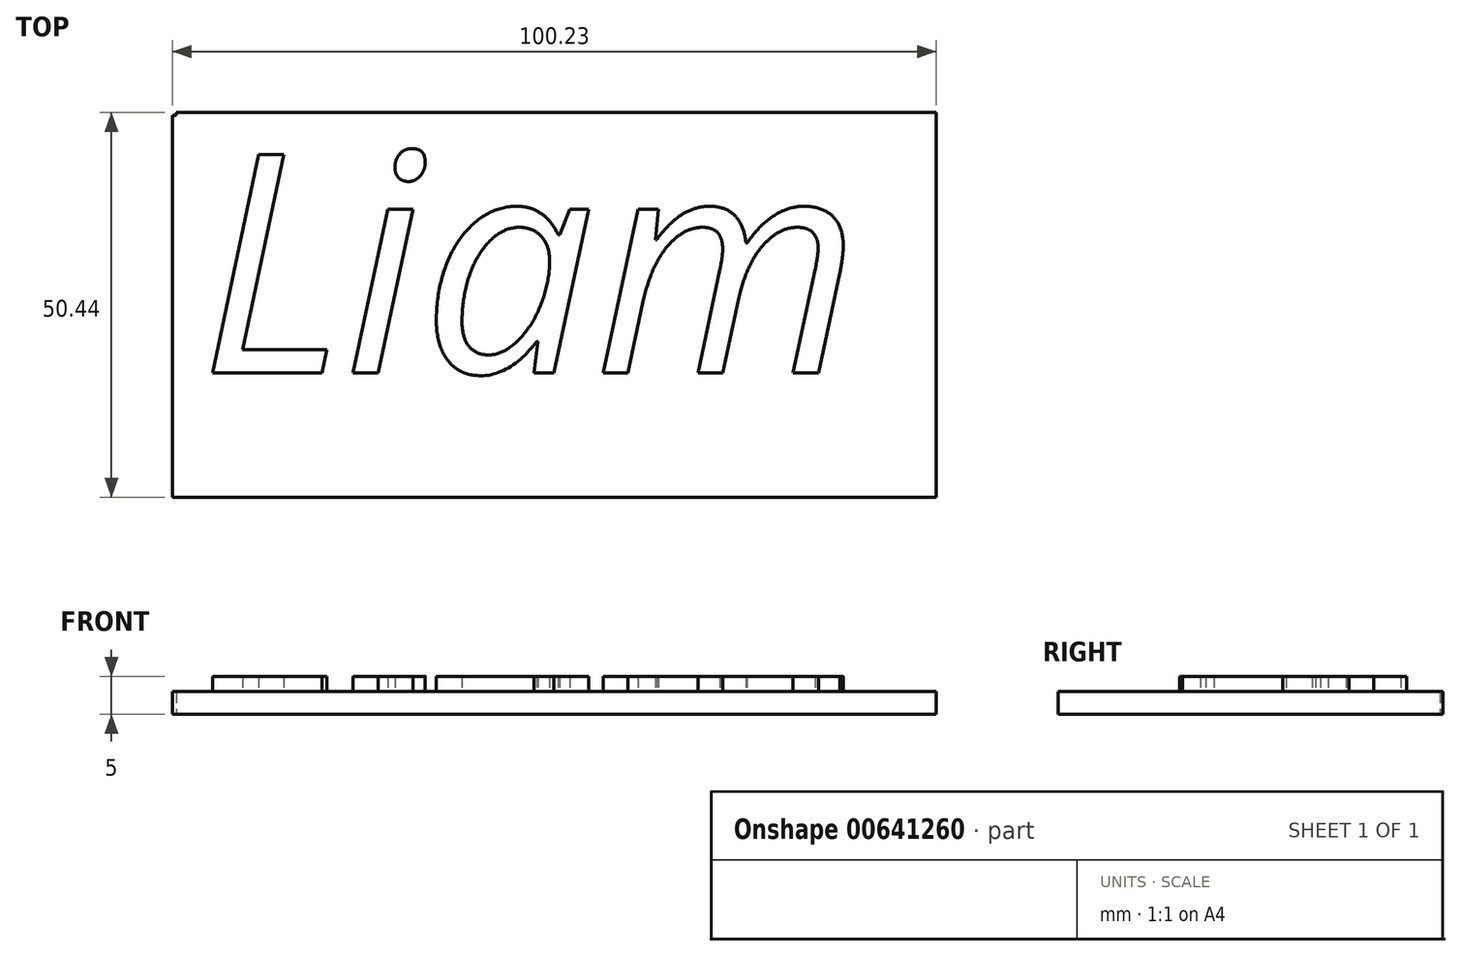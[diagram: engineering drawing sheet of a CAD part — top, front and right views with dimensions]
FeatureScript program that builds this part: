
annotation { "Feature Type Name" : "Feature", "Feature Type Description" : "" }
export const myFeature = defineFeature(function(context is Context, id is Id, definition is map)
    precondition{}
    {
        {
            var Q0;
            Q0=qCreatedBy(makeId("Top.planeOp"),FACE);
            var sketch = newSketch(context, id + "F0", { "sketchPlane" : qUnion([Q0])});
            skLineSegment(sketch, "E0.bottom", {"start": v(0, 0) * mm, "end": v(100.23, 0) * mm});
            skLineSegment(sketch, "E0.top", {"start": v(0, 50.1) * mm, "end": v(100.23, 50.1) * mm});
            skLineSegment(sketch, "E0.left", {"start": v(0, 0) * mm, "end": v(0, 50.1) * mm});
            skLineSegment(sketch, "E0.right", {"start": v(100.23, 0) * mm, "end": v(100.23, 50.1) * mm});
            skLineSegment(sketch, "E1.bottom", {"start": v(0.5, 0) * mm, "end": v(100.23, 0) * mm});
            skLineSegment(sketch, "E1.top", {"start": v(0.5, 50.44) * mm, "end": v(100.23, 50.44) * mm});
            skLineSegment(sketch, "E1.left", {"start": v(0.5, 0) * mm, "end": v(0.5, 50.44) * mm});
            skLineSegment(sketch, "E1.right", {"start": v(100.23, 0) * mm, "end": v(100.23, 50.44) * mm});
            skSolve(sketch);
        }
        {
            var Q0;
            Q0 = qSketchRegion(id + "F0", true);
            extrude(context, id + "F1", {"entities" : qUnion([Q0]), "depth" : 3 * mm, "offsetDistance" : 25 * mm});
        }
        {
            var Q0;
            Q0=makeQuery(id+"F1.opExtrude","CAP_FACE",FACE,{"disambiguationData":[OSD([sQuery(id+"F0.wireOp",EDGE,"E0.bottom"),sQuery(id+"F0.wireOp",EDGE,"E0.top"),sQuery(id+"F0.wireOp",EDGE,"E0.left"),sQuery(id+"F0.wireOp",EDGE,"E1.bottom"),sQuery(id+"F0.wireOp",EDGE,"E1.top"),sQuery(id+"F0.wireOp",EDGE,"E1.left"),sQuery(id+"F0.wireOp",EDGE,"E1.right")])],"isStart":false});
            var sketch = newSketch(context, id + "F2", { "sketchPlane" : qUnion([Q0])});
            skText(sketch, "E2", { "text": "Liam", "fontName": "OpenSans-Italic.ttf"});
            const initialGuessF2  = {"E2": [0.00357, 0.01633, 1, 0, 0.02883]};
            skSetInitialGuess(sketch, initialGuessF2);
            skSolve(sketch);
        }
        {
            var Q0;
            Q0 = qSketchRegion(id + "F2", true);
            extrude(context, id + "F3", {"entities" : qUnion([Q0]), "operationType" : NewBodyOperationType.ADD, "depth" : 2 * mm, "offsetDistance" : 25 * mm});
        }
    });
